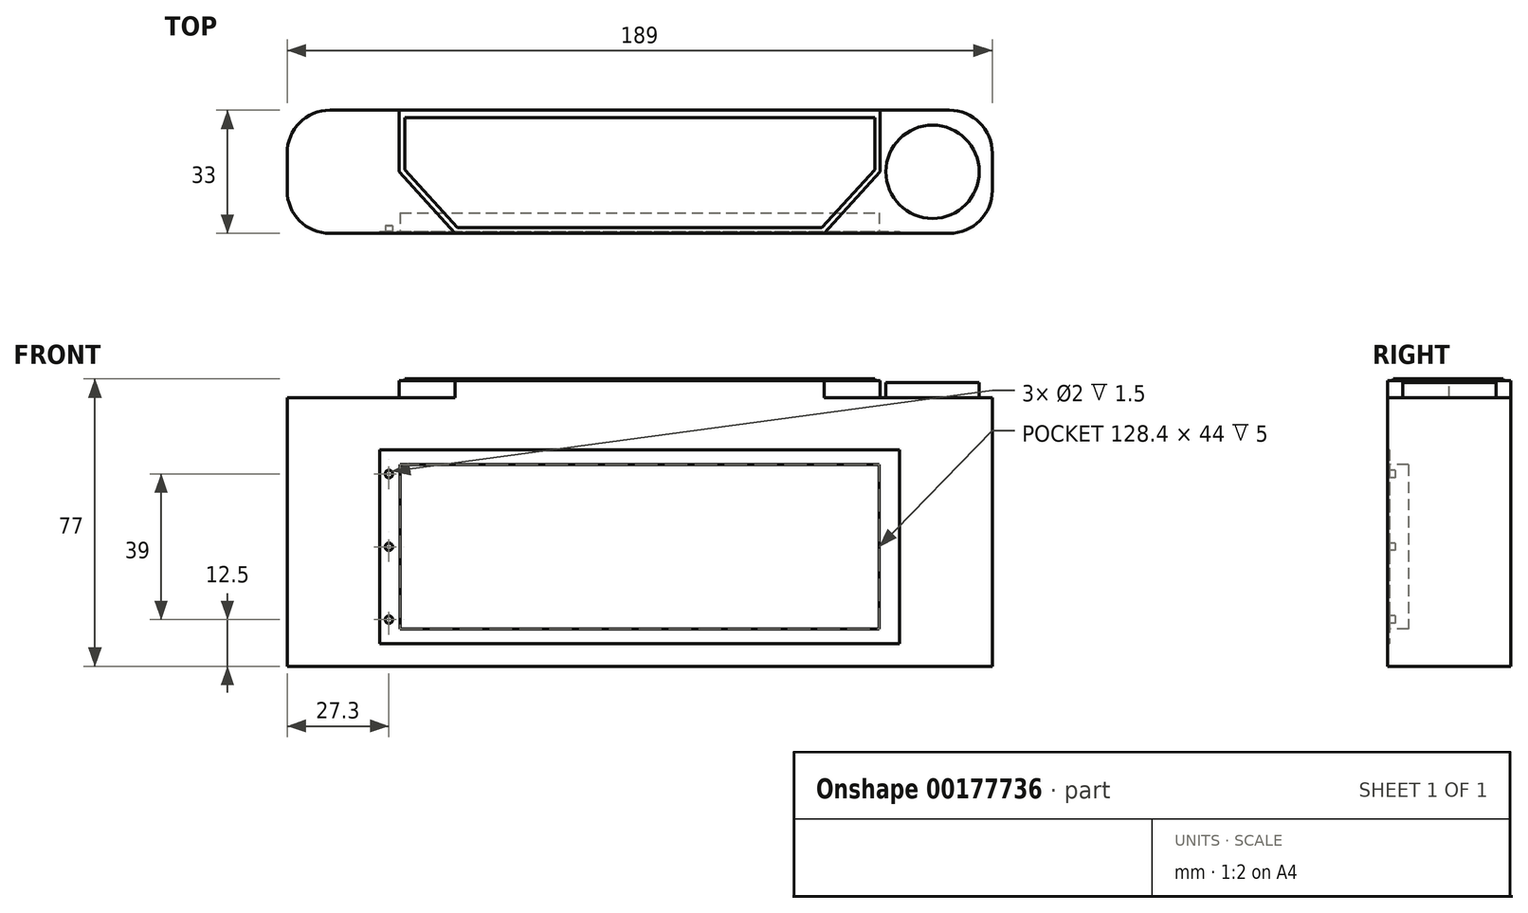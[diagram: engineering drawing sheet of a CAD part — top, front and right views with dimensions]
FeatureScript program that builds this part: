
annotation { "Feature Type Name" : "Feature", "Feature Type Description" : "" }
export const myFeature = defineFeature(function(context is Context, id is Id, definition is map)
    precondition{}
    {
        {
            var Q0;
            Q0=qCreatedBy(makeId("Front.planeOp"),FACE);
            var sketch = newSketch(context, id + "F0", { "sketchPlane" : qUnion([Q0])});
            skLineSegment(sketch, "E0", {"start": v(0, 0) * mm, "end": v(0, 38.5) * mm});
            skLineSegment(sketch, "E1", {"start": v(0, 38.5) * mm, "end": v(-94.5, 38.5) * mm});
            skLineSegment(sketch, "E2", {"start": v(-94.5, 38.5) * mm, "end": v(-64.5, 38.5) * mm});
            skLineSegment(sketch, "E3", {"start": v(-94.5, 38.5) * mm, "end": v(-94.5, 0) * mm});
            skLineSegment(sketch, "E4.MirrorCS", {"start": v(-94.5, -38.5) * mm, "end": v(-94.5, 0) * mm});
            skLineSegment(sketch, "E5.MirrorCS", {"start": v(0, 38.5) * mm, "end": v(94.5, 38.5) * mm});
            skLineSegment(sketch, "E6.MirrorCS", {"start": v(94.5, 38.5) * mm, "end": v(64.5, 38.5) * mm});
            skLineSegment(sketch, "E7.MirrorCS", {"start": v(94.5, 38.5) * mm, "end": v(94.5, 0) * mm});
            skLineSegment(sketch, "E8.MirrorCS", {"start": v(94.5, -38.5) * mm, "end": v(94.5, 0) * mm});
            skLineSegment(sketch, "E9.MirrorCS", {"start": v(0, -38.5) * mm, "end": v(94.5, -38.5) * mm});
            skLineSegment(sketch, "E10", {"start": v(-94.5, -38.5) * mm, "end": v(0, -38.5) * mm});
            skSolve(sketch);
        }
        {
            var Q0;
            Q0=makeQuery(id+"F0.imprint","IMPRINT",FACE,{"disambiguationData":[TD([[makeQuery(id+"F0.imprint","IMPRINT",EDGE,{"derivedFrom":sQuery(id+"F0.wireOp",EDGE,"E1")}),1.0]])]});
            extrude(context, id + "F1", {"entities" : qUnion([Q0]), "depth" : 33 * mm});
        }
        {
            var Q0;
            Q0=makeQuery(id+"F1.opExtrude","SWEPT_FACE",FACE,{"disambiguationData":[OSD([sQuery(id+"F0.wireOp",EDGE,"E1"),sQuery(id+"F0.wireOp",EDGE,"E2"),sQuery(id+"F0.wireOp",EDGE,"E5.MirrorCS"),sQuery(id+"F0.wireOp",EDGE,"E6.MirrorCS")])]});
            var sketch = newSketch(context, id + "F2", { "sketchPlane" : qUnion([Q0])});
            skLineSegment(sketch, "E11", {"start": v(-94.5, 0) * mm, "end": v(-94.5, -16.5) * mm});
            skLineSegment(sketch, "E12", {"start": v(-64.5, -16.5) * mm, "end": v(-64.5, -33) * mm});
            skLineSegment(sketch, "E13", {"start": v(-64.5, 0) * mm, "end": v(-49.5, 0) * mm});
            skLineSegment(sketch, "E14", {"start": v(-64.5, -16.5) * mm, "end": v(-49.5, 0) * mm});
            skLineSegment(sketch, "E15", {"start": v(-64.5, 0) * mm, "end": v(-94.5, 0) * mm});
            skLineSegment(sketch, "E16", {"start": v(-94.5, 0) * mm, "end": v(-94.5, -33) * mm});
            skLineSegment(sketch, "E17", {"start": v(-94.5, -33) * mm, "end": v(-64.5, -33) * mm});
            skLineSegment(sketch, "E18.MirrorCS", {"start": v(64.5, -16.5) * mm, "end": v(64.5, -33) * mm});
            skLineSegment(sketch, "E19.MirrorCS", {"start": v(64.5, -16.5) * mm, "end": v(49.5, 0) * mm});
            skLineSegment(sketch, "E20.MirrorCS", {"start": v(64.5, 0) * mm, "end": v(49.5, 0) * mm});
            skLineSegment(sketch, "E21.MirrorCS", {"start": v(64.5, 0) * mm, "end": v(94.5, 0) * mm});
            skLineSegment(sketch, "E22.MirrorCS", {"start": v(94.5, 0) * mm, "end": v(94.5, -33) * mm});
            skLineSegment(sketch, "E23.MirrorCS", {"start": v(94.5, -33) * mm, "end": v(64.5, -33) * mm});
            skSolve(sketch);
        }
        {
            var Q0;
            Q0 = qSketchRegion(id + "F2", true);
            extrude(context, id + "F3", {"entities" : qUnion([Q0]), "operationType" : NewBodyOperationType.REMOVE, "oppositeDirection" : true, "depth" : 5 * mm});
        }
        {
            var Q0;
            Q0=makeQuery(id+"F3.boolean.opBoolean","COPY",FACE,{"derivedFrom":makeQuery(id+"F3.opExtrude","CAP_FACE",FACE,{"disambiguationData":[OSD([sQuery(id+"F2.wireOp",EDGE,"E12"),sQuery(id+"F2.wireOp",EDGE,"E13"),sQuery(id+"F2.wireOp",EDGE,"E14"),sQuery(id+"F2.wireOp",EDGE,"E15"),sQuery(id+"F2.wireOp",EDGE,"E16"),sQuery(id+"F2.wireOp",EDGE,"E17")])],"isStart":false})});
            var sketch = newSketch(context, id + "F4", { "sketchPlane" : qUnion([Q0])});
            skLineSegment(sketch, "E24", {"start": v(-94.5, -33) * mm, "end": v(-94.5, -16.5) * mm});
            skLineSegment(sketch, "E25", {"start": v(-94.5, -16.5) * mm, "end": v(-91, -16.5) * mm});
            skLineSegment(sketch, "E26", {"start": v(-91, -16.5) * mm, "end": v(-78.5, -16.5) * mm});
            skCircle(sketch, "E27", {"center": v(-78.5, -16.5) * mm, "radius": 12.5 * mm});
            skCircle(sketch, "E28.MirrorC", {"center": v(78.5, -16.5) * mm, "radius": 12.5 * mm});
            skSolve(sketch);
        }
        {
            var Q0;
            Q0=makeQuery(id+"F4.imprint","IMPRINT",FACE,{"disambiguationData":[TD([[makeQuery(id+"F4.imprint","IMPRINT",EDGE,{"derivedFrom":sQuery(id+"F4.wireOp",EDGE,"E27")}),1.0]])]});
            var Q1;
            Q1=makeQuery(id+"F4.imprint","IMPRINT",FACE,{"disambiguationData":[TD([[makeQuery(id+"F4.imprint","IMPRINT",EDGE,{"derivedFrom":sQuery(id+"F4.wireOp",EDGE,"E28.MirrorC")}),-1.0]])]});
            extrude(context, id + "F5", {"entities" : qUnion([Q0, Q1]), "operationType" : NewBodyOperationType.ADD, "depth" : 4 * mm});
        }
        {
            var Q0;
            Q0=makeQuery(id+"F1.opExtrude","SWEPT_FACE",FACE,{"disambiguationData":[OSD([sQuery(id+"F0.wireOp",EDGE,"E1"),sQuery(id+"F0.wireOp",EDGE,"E2"),sQuery(id+"F0.wireOp",EDGE,"E5.MirrorCS"),sQuery(id+"F0.wireOp",EDGE,"E6.MirrorCS")])]});
            var sketch = newSketch(context, id + "F6", { "sketchPlane" : qUnion([Q0])});
            skLineSegment(sketch, "E29", {"start": v(0, 0) * mm, "end": v(0, -1.5) * mm});
            skPoint(sketch, "E29.endSnap0", {"position": v(0, 0) * mm});
            skLineSegment(sketch, "E30", {"start": v(0, -1.5) * mm, "end": v(48.84, -1.5) * mm});
            skLineSegment(sketch, "E31", {"start": v(48.84, -1.5) * mm, "end": v(63, -17.08) * mm});
            skLineSegment(sketch, "E32", {"start": v(63, -17.08) * mm, "end": v(63, -31) * mm});
            skLineSegment(sketch, "E33", {"start": v(63, -31) * mm, "end": v(0, -31) * mm});
            skLineSegment(sketch, "E34.MirrorCS", {"start": v(0, -1.5) * mm, "end": v(-48.84, -1.5) * mm});
            skLineSegment(sketch, "E35.MirrorCS", {"start": v(-48.84, -1.5) * mm, "end": v(-63, -17.08) * mm});
            skLineSegment(sketch, "E36.MirrorCS", {"start": v(-63, -17.08) * mm, "end": v(-63, -31) * mm});
            skLineSegment(sketch, "E37.MirrorCS", {"start": v(-63, -31) * mm, "end": v(0, -31) * mm});
            skLineSegment(sketch, "E38", {"start": v(0, -31) * mm, "end": v(0, -33) * mm});
            skSolve(sketch);
        }
        {
            var Q0;
            {var subQ6=sQuery(id+"F6.wireOp",EDGE,"E29");Q0=makeQuery(id+"F6.imprint","IMPRINT",FACE,{"disambiguationData":[TD([[makeQuery(id+"F6.imprint","IMPRINT",EDGE,{"derivedFrom":subQ6}),-1.0]])]});}
            var Q1;
            {var subQ0=sQuery(id+"F6.wireOp",EDGE,"E29");Q1=makeQuery(id+"F6.imprint","IMPRINT",FACE,{"disambiguationData":[TD([[makeQuery(id+"F6.imprint","IMPRINT",EDGE,{"derivedFrom":subQ0}),1.0]])]});}
            extrude(context, id + "F7", {"entities" : qUnion([Q0, Q1]), "operationType" : NewBodyOperationType.REMOVE, "oppositeDirection" : true, "depth" : 0.5 * mm});
        }
        {
            var Q0;
            Q0=makeQuery(id+"F1.opExtrude","CAP_EDGE",EDGE,{"disambiguationData":[OSD([sQuery(id+"F0.wireOp",EDGE,"E3"),sQuery(id+"F0.wireOp",EDGE,"E4.MirrorCS")])],"isStart":false});
            fillet(context, id + "F8", {"entities" : qUnion([Q0]), "radius" : 11.5 * mm, "tangentPropagation" : true, "allowEdgeOverflow" : false});
        }
        {
            var Q0;
            Q0=makeQuery(id+"F1.opExtrude","CAP_EDGE",EDGE,{"disambiguationData":[OSD([sQuery(id+"F0.wireOp",EDGE,"E3"),sQuery(id+"F0.wireOp",EDGE,"E4.MirrorCS")])],"isStart":true});
            var Q1;
            Q1=makeQuery(id+"F1.opExtrude","CAP_EDGE",EDGE,{"disambiguationData":[OSD([sQuery(id+"F0.wireOp",EDGE,"E7.MirrorCS"),sQuery(id+"F0.wireOp",EDGE,"E8.MirrorCS")])],"isStart":true});
            var Q2;
            Q2=makeQuery(id+"F1.opExtrude","CAP_EDGE",EDGE,{"disambiguationData":[OSD([sQuery(id+"F0.wireOp",EDGE,"E7.MirrorCS"),sQuery(id+"F0.wireOp",EDGE,"E8.MirrorCS")])],"isStart":false});
            fillet(context, id + "F9", {"entities" : qUnion([Q0, Q1, Q2]), "radius" : 11.5 * mm, "tangentPropagation" : true, "allowEdgeOverflow" : false});
        }
        {
            var Q0;
            Q0=qCreatedBy(makeId("Front.planeOp"),FACE);
            var sketch = newSketch(context, id + "F10", { "sketchPlane" : qUnion([Q0])});
            skLineSegment(sketch, "E39", {"start": v(69.7, 0) * mm, "end": v(69.7, -32.5) * mm});
            skLineSegment(sketch, "E40", {"start": v(69.7, -32.5) * mm, "end": v(0, -32.5) * mm});
            skLineSegment(sketch, "E41.MirrorCS", {"start": v(-69.7, 0) * mm, "end": v(-69.7, -32.5) * mm});
            skLineSegment(sketch, "E42.MirrorCS", {"start": v(-69.7, -32.5) * mm, "end": v(0, -32.5) * mm});
            skLineSegment(sketch, "E43", {"start": v(69.7, 0) * mm, "end": v(69.7, 19.5) * mm});
            skLineSegment(sketch, "E44", {"start": v(69.7, 19.5) * mm, "end": v(0, 19.5) * mm});
            skLineSegment(sketch, "E45.MirrorCS", {"start": v(-69.7, 0) * mm, "end": v(-69.7, 19.5) * mm});
            skLineSegment(sketch, "E46.MirrorCS", {"start": v(-69.7, 19.5) * mm, "end": v(0, 19.5) * mm});
            skSolve(sketch);
        }
        {
            var Q0;
            Q0 = qSketchRegion(id + "F10", true);
            extrude(context, id + "F11", {"entities" : qUnion([Q0]), "operationType" : NewBodyOperationType.REMOVE, "depth" : 0.5 * mm});
        }
        {
            var Q0;
            Q0=makeQuery(id+"F11.boolean.opBoolean","COPY",FACE,{"derivedFrom":makeQuery(id+"F11.opExtrude","CAP_FACE",FACE,{"disambiguationData":[OSD([sQuery(id+"F10.wireOp",EDGE,"E39"),sQuery(id+"F10.wireOp",EDGE,"E40"),sQuery(id+"F10.wireOp",EDGE,"E41.MirrorCS"),sQuery(id+"F10.wireOp",EDGE,"E42.MirrorCS"),sQuery(id+"F10.wireOp",EDGE,"E43"),sQuery(id+"F10.wireOp",EDGE,"E44"),sQuery(id+"F10.wireOp",EDGE,"E45.MirrorCS"),sQuery(id+"F10.wireOp",EDGE,"E46.MirrorCS")])],"isStart":false})});
            var sketch = newSketch(context, id + "F12", { "sketchPlane" : qUnion([Q0])});
            skLineSegment(sketch, "E47", {"start": v(-69.7, 0) * mm, "end": v(-64.2, 0) * mm});
            skLineSegment(sketch, "E48", {"start": v(-38, 19.5) * mm, "end": v(-38, 15.5) * mm});
            skLineSegment(sketch, "E49", {"start": v(-48.6, -32.5) * mm, "end": v(-48.6, -28.5) * mm});
            skLineSegment(sketch, "E50", {"start": v(-64.2, 15.5) * mm, "end": v(64.2, 15.5) * mm});
            skLineSegment(sketch, "E51", {"start": v(-64.2, -28.5) * mm, "end": v(64.2, -28.5) * mm});
            skLineSegment(sketch, "E52", {"start": v(-64.2, 15.5) * mm, "end": v(-64.2, -28.5) * mm});
            skLineSegment(sketch, "E53", {"start": v(64.2, 15.5) * mm, "end": v(64.2, -28.5) * mm});
            skLineSegment(sketch, "E54", {"start": v(-69.7, 19.5) * mm, "end": v(-67.2, 19.5) * mm});
            skLineSegment(sketch, "E55", {"start": v(-67.2, 19.5) * mm, "end": v(-67.2, 13) * mm});
            skLineSegment(sketch, "E56", {"start": v(-67.2, 0) * mm, "end": v(-67.2, -6.5) * mm});
            skPoint(sketch, "E56.startSnap0", {"position": v(-66.95, 0) * mm});
            skLineSegment(sketch, "E57", {"start": v(-67.2, -32.5) * mm, "end": v(-67.2, -26) * mm});
            skCircle(sketch, "E58", {"center": v(-67.2, -26) * mm, "radius": 1 * mm});
            skCircle(sketch, "E59", {"center": v(-67.2, -6.5) * mm, "radius": 1 * mm});
            skCircle(sketch, "E60", {"center": v(-67.2, 13) * mm, "radius": 1 * mm});
            skCircle(sketch, "E61.MirrorC", {"center": v(67.2, 13) * mm, "radius": 1 * mm});
            skCircle(sketch, "E62.MirrorC", {"center": v(67.2, -6.5) * mm, "radius": 1 * mm});
            skCircle(sketch, "E63.MirrorC", {"center": v(67.2, -26) * mm, "radius": 1 * mm});
            skSolve(sketch);
        }
        {
            var Q0;
            {var subQ6=sQuery(id+"F12.wireOp",EDGE,"E53");Q0=makeQuery(id+"F12.imprint","IMPRINT",FACE,{"disambiguationData":[TD([[makeQuery(id+"F12.imprint","IMPRINT",EDGE,{"derivedFrom":subQ6}),-1.0]])]});}
            extrude(context, id + "F13", {"entities" : qUnion([Q0]), "operationType" : NewBodyOperationType.REMOVE, "oppositeDirection" : true, "depth" : 5 * mm});
        }
        {
            var Q0;
            Q0=makeQuery(id+"F12.imprint","IMPRINT",FACE,{"disambiguationData":[TD([[makeQuery(id+"F12.imprint","IMPRINT",EDGE,{"derivedFrom":sQuery(id+"F12.wireOp",EDGE,"E60")}),1.0]])]});
            var Q1;
            Q1=makeQuery(id+"F12.imprint","IMPRINT",FACE,{"disambiguationData":[TD([[makeQuery(id+"F12.imprint","IMPRINT",EDGE,{"derivedFrom":sQuery(id+"F12.wireOp",EDGE,"E59")}),1.0]])]});
            var Q2;
            Q2=makeQuery(id+"F12.imprint","IMPRINT",FACE,{"disambiguationData":[TD([[makeQuery(id+"F12.imprint","IMPRINT",EDGE,{"derivedFrom":sQuery(id+"F12.wireOp",EDGE,"E63.MirrorC")}),-1.0]])]});
            var Q3;
            Q3=makeQuery(id+"F12.imprint","IMPRINT",FACE,{"disambiguationData":[TD([[makeQuery(id+"F12.imprint","IMPRINT",EDGE,{"derivedFrom":sQuery(id+"F12.wireOp",EDGE,"E62.MirrorC")}),-1.0]])]});
            var Q4;
            Q4=makeQuery(id+"F12.imprint","IMPRINT",FACE,{"disambiguationData":[TD([[makeQuery(id+"F12.imprint","IMPRINT",EDGE,{"derivedFrom":sQuery(id+"F12.wireOp",EDGE,"E61.MirrorC")}),-1.0]])]});
            var Q5;
            Q5=makeQuery(id+"F12.imprint","IMPRINT",FACE,{"disambiguationData":[TD([[makeQuery(id+"F12.imprint","IMPRINT",EDGE,{"derivedFrom":sQuery(id+"F12.wireOp",EDGE,"E58")}),1.0]])]});
            extrude(context, id + "F14", {"entities" : qUnion([Q0, Q1, Q2, Q3, Q4, Q5]), "operationType" : NewBodyOperationType.REMOVE, "oppositeDirection" : true, "depth" : 1.5 * mm});
        }
        {
            var Q0;
            Q0=makeQuery(id+"F1.opExtrude","SWEPT_BODY",BODY,{"disambiguationData":[OSD([sQuery(id+"F0.wireOp",EDGE,"E1"),sQuery(id+"F0.wireOp",EDGE,"E2"),sQuery(id+"F0.wireOp",EDGE,"E3"),sQuery(id+"F0.wireOp",EDGE,"E4.MirrorCS"),sQuery(id+"F0.wireOp",EDGE,"E5.MirrorCS"),sQuery(id+"F0.wireOp",EDGE,"E6.MirrorCS"),sQuery(id+"F0.wireOp",EDGE,"E7.MirrorCS"),sQuery(id+"F0.wireOp",EDGE,"E8.MirrorCS"),sQuery(id+"F0.wireOp",EDGE,"E9.MirrorCS"),sQuery(id+"F0.wireOp",EDGE,"E10")])]});
            var Q1;
            {var subQ0=sQuery(id+"F0.wireOp",EDGE,"E8.MirrorCS");var subQ1=sQuery(id+"F0.wireOp",EDGE,"E7.MirrorCS");Q1=makeQuery(id+"F9.opFillet","BLEND_EDGE",EDGE,{"blendedFrom":[makeQuery(id+"F1.opExtrude","CAP_EDGE",EDGE,{"disambiguationData":[OSD([subQ1,subQ0])],"isStart":true}),makeQuery(id+"F1.opExtrude","CAP_FACE",FACE,{"disambiguationData":[OSD([sQuery(id+"F0.wireOp",EDGE,"E1"),sQuery(id+"F0.wireOp",EDGE,"E2"),sQuery(id+"F0.wireOp",EDGE,"E3"),sQuery(id+"F0.wireOp",EDGE,"E4.MirrorCS"),sQuery(id+"F0.wireOp",EDGE,"E5.MirrorCS"),sQuery(id+"F0.wireOp",EDGE,"E6.MirrorCS"),subQ1,subQ0,sQuery(id+"F0.wireOp",EDGE,"E9.MirrorCS"),sQuery(id+"F0.wireOp",EDGE,"E10")])],"isStart":true})],"blendedInto":[makeQuery(id+"F1.opExtrude","CAP_FACE",FACE,{"disambiguationData":[OSD([sQuery(id+"F0.wireOp",EDGE,"E1"),sQuery(id+"F0.wireOp",EDGE,"E2"),sQuery(id+"F0.wireOp",EDGE,"E3"),sQuery(id+"F0.wireOp",EDGE,"E4.MirrorCS"),sQuery(id+"F0.wireOp",EDGE,"E5.MirrorCS"),sQuery(id+"F0.wireOp",EDGE,"E6.MirrorCS"),subQ1,subQ0,sQuery(id+"F0.wireOp",EDGE,"E9.MirrorCS"),sQuery(id+"F0.wireOp",EDGE,"E10")])],"isStart":true})]});}
            transform(context, id + "F15", {"entities" : qUnion([Q0]), "transformType" : TransformType.ROTATION, "transformAxis" : qUnion([Q1]), "angle" : 180 * degree, "makeCopy" : false});
        }
        {
            var Q0;
            Q0=makeQuery(id+"F1.opExtrude","SWEPT_BODY",BODY,{"disambiguationData":[OSD([sQuery(id+"F0.wireOp",EDGE,"E1"),sQuery(id+"F0.wireOp",EDGE,"E2"),sQuery(id+"F0.wireOp",EDGE,"E3"),sQuery(id+"F0.wireOp",EDGE,"E4.MirrorCS"),sQuery(id+"F0.wireOp",EDGE,"E5.MirrorCS"),sQuery(id+"F0.wireOp",EDGE,"E6.MirrorCS"),sQuery(id+"F0.wireOp",EDGE,"E7.MirrorCS"),sQuery(id+"F0.wireOp",EDGE,"E8.MirrorCS"),sQuery(id+"F0.wireOp",EDGE,"E9.MirrorCS"),sQuery(id+"F0.wireOp",EDGE,"E10")])]});
            var Q1;
            Q1=makeQuery(id+"F1.opExtrude","CAP_EDGE",EDGE,{"disambiguationData":[OSD([sQuery(id+"F0.wireOp",EDGE,"E9.MirrorCS"),sQuery(id+"F0.wireOp",EDGE,"E10")])],"isStart":true});
            transform(context, id + "F16", {"entities" : qUnion([Q0]), "transformType" : TransformType.TRANSLATION_ENTITY, "oppositeDirectionEntity" : false, "transformLine" : qUnion([Q1]), "makeCopy" : false});
        }
    });
